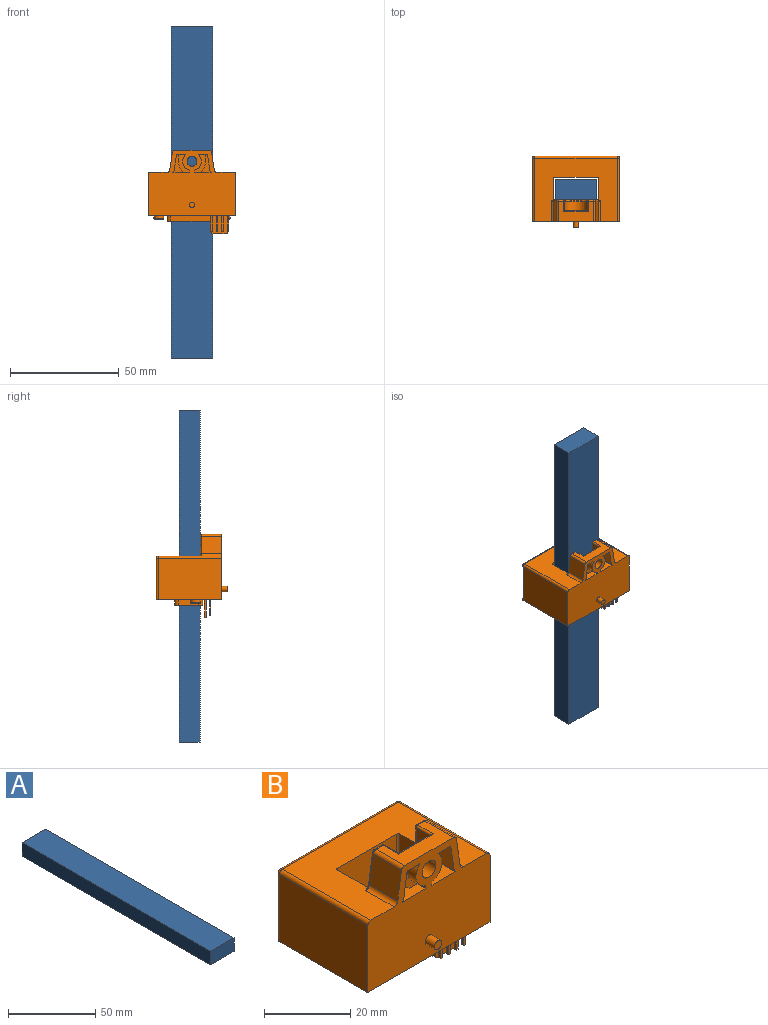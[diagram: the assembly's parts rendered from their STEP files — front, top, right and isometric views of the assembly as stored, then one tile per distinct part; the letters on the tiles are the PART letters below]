
ASSEMBLY  parts=2 mates=1
PART A: 6 faces, bbox 19.1x152.4x9.5 mm
  f0: plane 152.4x19.05mm, normal (0,0,1), area 2903.2mm2, adj f1,f3,f4,f5
  f1: plane 152.4x9.53mm, normal (-1,0,0), area 1451.6mm2, adj f0,f2,f4,f5
  f2: plane 152.4x19.05mm, normal (0,0,-1), area 2903.2mm2, adj f1,f3,f4,f5
  f3: plane 152.4x9.53mm, normal (1,0,0), area 1451.6mm2, adj f0,f2,f4,f5
  f4: plane 19.05x9.53mm, normal (0,-1,0), area 181.5mm2, adj f0,f1,f2,f3
  f5: plane 19.05x9.53mm, normal (0,1,0), area 181.5mm2, adj f0,f1,f2,f3
PART B: 152 faces, bbox 40.2x33.2x38.6 mm
  f0: plane 2.5x2.5mm, normal (0,-1,0), area 4.9mm2, adj f53
  f1: plane 9.4x2.5mm, normal (1,0,0), area 23.5mm2, adj f8,f65,f73,f78
  f2: plane 5x3mm, normal (-1,0,0), area 15mm2, adj f4,f12,f51,f76
  f3: cylinder r=5.2mm len=10.4mm, axis (0,1,0), area 73.5mm2, adj f5,f10,f15,f75
  f4: plane 8x5.1mm, normal (0,-1,0), area 16.1mm2, adj f2,f51,f56,f59,f62,f68,f76
  f5: torus R=5.7mm, axis (0,-1,0), area 13.3mm2, adj f3,f29,f77,f82
  f6: torus R=0.5mm, axis (0,-1,0), area 0.9mm2, adj f16,f29,f54,f81
  f7: plane 19.4x2.5mm, normal (0,1,0), area 48.5mm2, adj f8,f65,f78,f85
  f8: plane 40x30mm, normal (0,0,-1), area 818.2mm2, adj f1,f7,f9,f19,f20,f21,f22,f23
  f9: cylinder r=1.7mm len=2.5mm, axis (0,0,1), area 6.7mm2, adj f8,f65,f72,f79
  f10: plane 10.4x9.7mm, normal (0,1,0), area 73.4mm2, adj f3,f15,f36,f48,f75
  f11: plane 4.2x4.2mm, normal (0,0,-1), area 13.9mm2, adj f74
  f12: plane 8x5.2mm, normal (0,-1,0), area 19.2mm2, adj f2,f51,f52,f55,f68,f76
  f13: cylinder r=0.5mm len=22.5mm, axis (0,0,1), area 17.7mm2, adj f33,f47,f65,f71
  f14: plane 8x5.2mm, normal (0,-1,0), area 19.2mm2, adj f34,f49,f50,f57,f67,f83
  f15: plane 4.5x4.5mm, normal (1,0,0), area 20.2mm2, adj f3,f10,f17,f82
  f16: cylinder r=0.5mm len=2.3mm, axis (1,0,0), area 1.8mm2, adj f6,f29,f64,f70
  f17: cylinder r=0.5mm len=5mm, axis (0,-1,0), area 3.7mm2, adj f15,f36,f61,f64
  f18: torus R=0.5mm, axis (0,-1,0), area 0.9mm2, adj f29,f35,f37,f63
  f19: plane 29x19mm, normal (1,0,0), area 551mm2, adj f8,f21,f23,f39
  f20: plane 29x19mm, normal (-1,0,0), area 551mm2, adj f8,f22,f23,f40
  f21: cylinder r=1mm len=19mm, axis (0,0,-1), area 29.8mm2, adj f8,f19,f24,f41
  f22: cylinder r=1mm len=19mm, axis (0,0,-1), area 29.8mm2, adj f8,f20,f24,f42
  f23: plane 40x30mm, normal (0,-1,0), area 900.4mm2, adj f8,f19,f20,f39,f40,f43,f44,f45
  f24: plane 38x19mm, normal (0,1,0), area 722mm2, adj f8,f21,f22,f69
  f25: torus R=1.71mm, axis (0,-1,0), area 1.1mm2, adj f29,f43,f47,f81
  f26: torus R=1.71mm, axis (0,-1,0), area 1.1mm2, adj f29,f35,f46,f47
  f27: plane 8x5.1mm, normal (0,-1,0), area 16.1mm2, adj f34,f44,f45,f57,f58,f67,f83
  f28: plane 22.5x9.4mm, normal (1,0,0), area 211.5mm2, adj f30,f32,f47,f65
  f29: plane 32x20.38mm, normal (0,1,0), area 508mm2, adj f5,f6,f16,f18,f25,f26,f31,f32
  f30: cylinder r=0.5mm len=22.5mm, axis (0,0,1), area 17.7mm2, adj f28,f33,f47,f65
  f31: cylinder r=0.5mm len=22.5mm, axis (0,0,1), area 17.7mm2, adj f29,f47,f65,f71
  f32: cylinder r=0.5mm len=22.5mm, axis (0,0,1), area 17.7mm2, adj f28,f29,f47,f65
  f33: plane 22.5x19.4mm, normal (0,-1,0), area 436.5mm2, adj f13,f30,f47,f65
  f34: cylinder r=6.2mm len=5mm, axis (0,-1,0), area 29.1mm2, adj f14,f27,f57,f83
  f35: cylinder r=0.5mm len=8.19mm, axis (0.15,0,0.99), area 6.4mm2, adj f18,f26,f29,f60
  f36: cylinder r=0.5mm len=11.4mm, axis (-1,0,0), area 8.6mm2, adj f10,f17,f38,f64
  f37: cylinder r=0.5mm len=2.3mm, axis (1,0,0), area 1.8mm2, adj f18,f29,f61,f64
  f38: cylinder r=0.5mm len=5mm, axis (0,-1,0), area 3.7mm2, adj f36,f64,f70,f75
  f39: cylinder r=1mm len=29mm, axis (0,1,0), area 45.6mm2, adj f19,f23,f41,f47
  f40: cylinder r=1mm len=29mm, axis (0,-1,0), area 45.6mm2, adj f20,f23,f42,f47
  f41: sphere r=1mm, area 1.6mm2, adj f21,f39,f69
  f42: sphere r=1mm, area 1.6mm2, adj f22,f40,f69
  f43: cylinder r=1.21mm len=9.3mm, axis (0,-1,0), area 16.1mm2, adj f23,f25,f47,f66
  f44: cylinder r=0.5mm len=7.8mm, axis (0,-1,0), area 5.5mm2, adj f23,f27,f58,f67
  f45: cylinder r=0.5mm len=7.8mm, axis (0,-1,0), area 5.5mm2, adj f23,f27,f57,f58
  f46: cylinder r=1.21mm len=9.3mm, axis (0,-1,0), area 16.1mm2, adj f23,f26,f47,f60
  f47: plane 38.17x29.17mm, normal (0,0,1), area 667mm2, adj f13,f23,f25,f26,f28,f29,f30,f31
  f48: cylinder r=2.25mm len=4.8mm, axis (0,-1,0), area 67.9mm2, adj f10,f23
  f49: plane 2.8x0.87mm, normal (1,0,0), area 2.4mm2, adj f14,f23,f50,f57
  f50: cylinder r=4.25mm len=7.13mm, axis (0,-1,0), area 25.2mm2, adj f14,f23,f49,f67
  f51: plane 7.8x3.7mm, normal (0,0,-1), area 12.9mm2, adj f2,f4,f12,f23,f55,f62
  f52: plane 2.8x0.87mm, normal (-1,0,0), area 2.4mm2, adj f12,f23,f55,f68
  f53: cylinder r=1.25mm len=3mm, axis (0,1,0), area 23.6mm2, adj f0,f23
  f54: cylinder r=1mm len=9.3mm, axis (0,-1,0), area 13.2mm2, adj f6,f23,f64,f66
  f55: cylinder r=4.25mm len=7.13mm, axis (0,-1,0), area 25.2mm2, adj f12,f23,f51,f52
  f56: cylinder r=0.5mm len=7.8mm, axis (0,-1,0), area 5.5mm2, adj f4,f23,f59,f68
  f57: plane 7.8x7.76mm, normal (0,0,1), area 47.2mm2, adj f14,f23,f27,f34,f45,f49
  f58: plane 7.8x7.15mm, normal (-0.99,0,-0.15), area 56.4mm2, adj f23,f27,f44,f45
  f59: plane 7.8x7.15mm, normal (0.99,0,-0.15), area 56.4mm2, adj f4,f23,f56,f62
  f60: plane 9.3x8.11mm, normal (-0.99,0,0.15), area 76.3mm2, adj f23,f35,f46,f63
  f61: sphere r=0.5mm, area 0.4mm2, adj f17,f37,f82
  f62: cylinder r=0.5mm len=7.8mm, axis (0,-1,0), area 5.5mm2, adj f4,f23,f51,f59
  f63: cylinder r=1mm len=9.3mm, axis (0,-1,0), area 13.2mm2, adj f18,f23,f60,f64
  f64: plane 16x9.3mm, normal (0,0,1), area 91.8mm2, adj f16,f17,f23,f36,f37,f38,f54,f63
  f65: plane 22.8x12.8mm, normal (0,0,-1), area 77.4mm2, adj f1,f7,f9,f13,f28,f29,f30,f31
  f66: plane 9.3x8.11mm, normal (0.99,0,0.15), area 76.3mm2, adj f23,f43,f54,f81
  f67: plane 7.8x3.7mm, normal (0,0,-1), area 12.9mm2, adj f14,f23,f27,f44,f50,f83
  f68: plane 7.8x7.76mm, normal (0,0,1), area 47.2mm2, adj f4,f12,f23,f52,f56,f76
  f69: cylinder r=1mm len=38mm, axis (-1,0,0), area 59.7mm2, adj f24,f41,f42,f47
  f70: sphere r=0.5mm, area 0.4mm2, adj f16,f38,f77
  f71: plane 22.5x9.4mm, normal (-1,0,0), area 211.5mm2, adj f13,f31,f47,f65
  f72: plane 9.4x2.5mm, normal (-1,0,0), area 23.5mm2, adj f8,f9,f65,f85
  f73: cylinder r=1.7mm len=2.5mm, axis (0,0,1), area 6.7mm2, adj f1,f8,f65,f79
  f74: cone r=2.3mm half-angle=45deg, axis (0,0,1), area 3.9mm2, adj f11,f84
  f75: plane 4.5x4.5mm, normal (-1,0,0), area 20.2mm2, adj f3,f10,f38,f77
  f76: cylinder r=6.2mm len=5mm, axis (0,-1,0), area 29.1mm2, adj f2,f4,f12,f68
  f77: cylinder r=0.5mm len=4.5mm, axis (0,0,-1), area 3.5mm2, adj f5,f29,f70,f75
  f78: cylinder r=1.7mm len=2.5mm, axis (0,0,1), area 6.7mm2, adj f1,f7,f8,f65
  f79: plane 19.4x2.5mm, normal (0,-1,0), area 48.5mm2, adj f8,f9,f65,f73
  f80: plane 9.8x6mm, normal (0,0,-1), area 3.7mm2, adj f86,f90,f91,f92,f93,f94,f95,f96
  f81: cylinder r=0.5mm len=8.19mm, axis (0.15,0,-0.99), area 6.4mm2, adj f6,f25,f29,f66
  f82: cylinder r=0.5mm len=4.5mm, axis (0,0,1), area 3.5mm2, adj f5,f15,f29,f61
  f83: plane 5x3mm, normal (1,0,0), area 15mm2, adj f14,f27,f34,f67
  f84: cylinder r=2.3mm len=4.6mm, axis (0,0,1), area 18.8mm2, adj f8,f74
  f85: cylinder r=1.7mm len=2.5mm, axis (0,0,1), area 6.7mm2, adj f7,f8,f65,f72
  f86: plane 6x3.3mm, normal (-1,0,0), area 19.8mm2, adj f8,f80,f90,f92
  f87: cylinder r=2.3mm len=4.6mm, axis (0,0,1), area 18.8mm2, adj f8,f88
  f88: cone r=2.3mm half-angle=45deg, axis (0,0,1), area 3.9mm2, adj f87,f89
  f89: plane 4.2x4.2mm, normal (0,0,-1), area 13.9mm2, adj f88
  f90: plane 9.8x3.3mm, normal (0,-1,0), area 32.3mm2, adj f8,f80,f86,f91
  f91: plane 6x3.3mm, normal (1,0,0), area 19.8mm2, adj f8,f80,f90,f92
  f92: plane 9.8x3.3mm, normal (0,1,0), area 32.3mm2, adj f8,f80,f86,f91
  f93: plane 5.8x3.2mm, normal (-1,0,0), area 18.6mm2, adj f80,f94,f96,f97
  f94: plane 9.5x3.2mm, normal (0,-1,0), area 30.4mm2, adj f80,f93,f95,f97
  f95: plane 5.8x3.2mm, normal (1,0,0), area 18.6mm2, adj f80,f94,f96,f97
  f96: plane 11.6x9.5mm, normal (0,1,0), area 93.2mm2, adj f80,f93,f95,f97,f116,f117,f118,f119
  f97: plane 9.5x5.8mm, normal (0,0,-1), area 47.1mm2, adj f93,f94,f95,f96,f99,f100,f105,f106
  f98: plane 0.64x0.2mm, normal (0.71,0,-0.71), area 0.1mm2, adj f99,f102,f103,f104
  f99: plane 7.3x0.64mm, normal (1,0,0), area 4.7mm2, adj f97,f98,f100,f105
  f100: plane 7.3x0.64mm, normal (0,1,0), area 4.7mm2, adj f97,f99,f102,f106
  f101: plane 0.64x0.2mm, normal (-0.71,0,-0.71), area 0.1mm2, adj f102,f103,f104,f106
  f102: plane 0.64x0.2mm, normal (0,0.71,-0.71), area 0.1mm2, adj f98,f100,f101,f103
  f103: plane 0.24x0.24mm, normal (0,0,-1), area 0.1mm2, adj f98,f101,f102,f104
  f104: plane 0.64x0.2mm, normal (0,-0.71,-0.71), area 0.1mm2, adj f98,f101,f103,f105
  f105: plane 7.3x0.64mm, normal (0,-1,0), area 4.7mm2, adj f97,f99,f104,f106
  f106: plane 7.3x0.64mm, normal (-1,0,0), area 4.7mm2, adj f97,f100,f101,f105
  f107: plane 0.64x0.2mm, normal (0,-0.71,-0.71), area 0.1mm2, adj f108,f113,f114,f115
  f108: plane 7.3x0.64mm, normal (0,-1,0), area 4.7mm2, adj f97,f107,f109,f112
  f109: plane 7.3x0.64mm, normal (-1,0,0), area 4.7mm2, adj f97,f108,f111,f115
  f110: plane 0.64x0.2mm, normal (0,0.71,-0.71), area 0.1mm2, adj f111,f113,f114,f115
  f111: plane 7.3x0.64mm, normal (0,1,0), area 4.7mm2, adj f97,f109,f110,f112
  f112: plane 7.3x0.64mm, normal (1,0,0), area 4.7mm2, adj f97,f108,f111,f113
  f113: plane 0.64x0.2mm, normal (0.71,0,-0.71), area 0.1mm2, adj f107,f110,f112,f114
  f114: plane 0.24x0.24mm, normal (0,0,-1), area 0.1mm2, adj f107,f110,f113,f115
  f115: plane 0.64x0.2mm, normal (-0.71,0,-0.71), area 0.1mm2, adj f107,f109,f110,f114
  f116: plane 8.11x0.85mm, normal (1,0,0), area 6.9mm2, adj f96,f97,f117,f121
  f117: plane 0.85x0.8mm, normal (0.34,0,-0.94), area 0.7mm2, adj f96,f116,f118,f121
  f118: plane 5.9x0.85mm, normal (0,0,-1), area 5mm2, adj f96,f117,f119,f121
  f119: plane 0.85x0.8mm, normal (-0.34,0,-0.94), area 0.7mm2, adj f96,f118,f120,f121
  f120: plane 8.11x0.85mm, normal (-1,0,0), area 6.9mm2, adj f96,f97,f119,f121
  f121: plane 8.4x7.5mm, normal (0,-1,0), area 62.8mm2, adj f97,f116,f117,f118,f119,f120
  f122: plane 0.64x0.2mm, normal (-0.71,0,-0.71), area 0.1mm2, adj f123,f124,f125,f127
  f123: plane 0.64x0.2mm, normal (0,0.71,-0.71), area 0.1mm2, adj f122,f124,f128,f130
  f124: plane 0.24x0.24mm, normal (0,0,-1), area 0.1mm2, adj f122,f123,f125,f130
  f125: plane 0.64x0.2mm, normal (0,-0.71,-0.71), area 0.1mm2, adj f122,f124,f126,f130
  f126: plane 7.3x0.64mm, normal (0,-1,0), area 4.7mm2, adj f97,f125,f127,f129
  f127: plane 7.3x0.64mm, normal (-1,0,0), area 4.7mm2, adj f97,f122,f126,f128
  f128: plane 7.3x0.64mm, normal (0,1,0), area 4.7mm2, adj f97,f123,f127,f129
  f129: plane 7.3x0.64mm, normal (1,0,0), area 4.7mm2, adj f97,f126,f128,f130
  f130: plane 0.64x0.2mm, normal (0.71,0,-0.71), area 0.1mm2, adj f123,f124,f125,f129
  f131: plane 0.64x0.2mm, normal (0.71,0,-0.71), area 0.1mm2, adj f132,f134,f135,f136
  f132: plane 7.3x0.64mm, normal (1,0,0), area 4.7mm2, adj f97,f131,f133,f138
  f133: plane 7.3x0.64mm, normal (0,1,0), area 4.7mm2, adj f97,f132,f136,f139
  f134: plane 0.64x0.2mm, normal (0,-0.71,-0.71), area 0.1mm2, adj f131,f135,f137,f138
  f135: plane 0.24x0.24mm, normal (0,0,-1), area 0.1mm2, adj f131,f134,f136,f137
  f136: plane 0.64x0.2mm, normal (0,0.71,-0.71), area 0.1mm2, adj f131,f133,f135,f137
  f137: plane 0.64x0.2mm, normal (-0.71,0,-0.71), area 0.1mm2, adj f134,f135,f136,f139
  f138: plane 7.3x0.64mm, normal (0,-1,0), area 4.7mm2, adj f97,f132,f134,f139
  f139: plane 7.3x0.64mm, normal (-1,0,0), area 4.7mm2, adj f97,f133,f137,f138
  f140: plane 6x4mm, normal (0,0,-1), area 24mm2, adj f141,f143,f144,f145
  f141: plane 6x1.6mm, normal (-1,0,0), area 9.6mm2, adj f140,f142,f143,f145
  f142: plane 6x4mm, normal (0,0,1), area 24mm2, adj f141,f143,f144,f145
  f143: plane 4x1.6mm, normal (0,1,0), area 6.4mm2, adj f140,f141,f142,f144
  f144: plane 6x1.6mm, normal (1,0,0), area 9.6mm2, adj f140,f142,f143,f145
  f145: plane 4x1.6mm, normal (0,-1,0), area 6.4mm2, adj f140,f141,f142,f144
  f146: plane 2x2mm, normal (0,0,-1), area 3.1mm2, adj f147
  f147: cylinder r=1mm len=3.6mm, axis (0,0,1), area 22.6mm2, adj f146,f148
  f148: plane 2x2mm, normal (0,0,1), area 3.1mm2, adj f147
  f149: plane 2x2mm, normal (0,0,-1), area 3.1mm2, adj f150
  f150: cylinder r=1mm len=3.6mm, axis (0,0,1), area 22.6mm2, adj f149,f151
  f151: plane 2x2mm, normal (0,0,1), area 3.1mm2, adj f150
PLACE A rot(axis=(1,0,0),90deg) t=(-24.62,-27.77,56.74)mm
PLACE B t=(-44.62,-42.33,-32.89)mm
MATE planar A.f0 <-> B.f29  axis (0,-1,0) through (-24.62,-32.53,-19.46)mm
